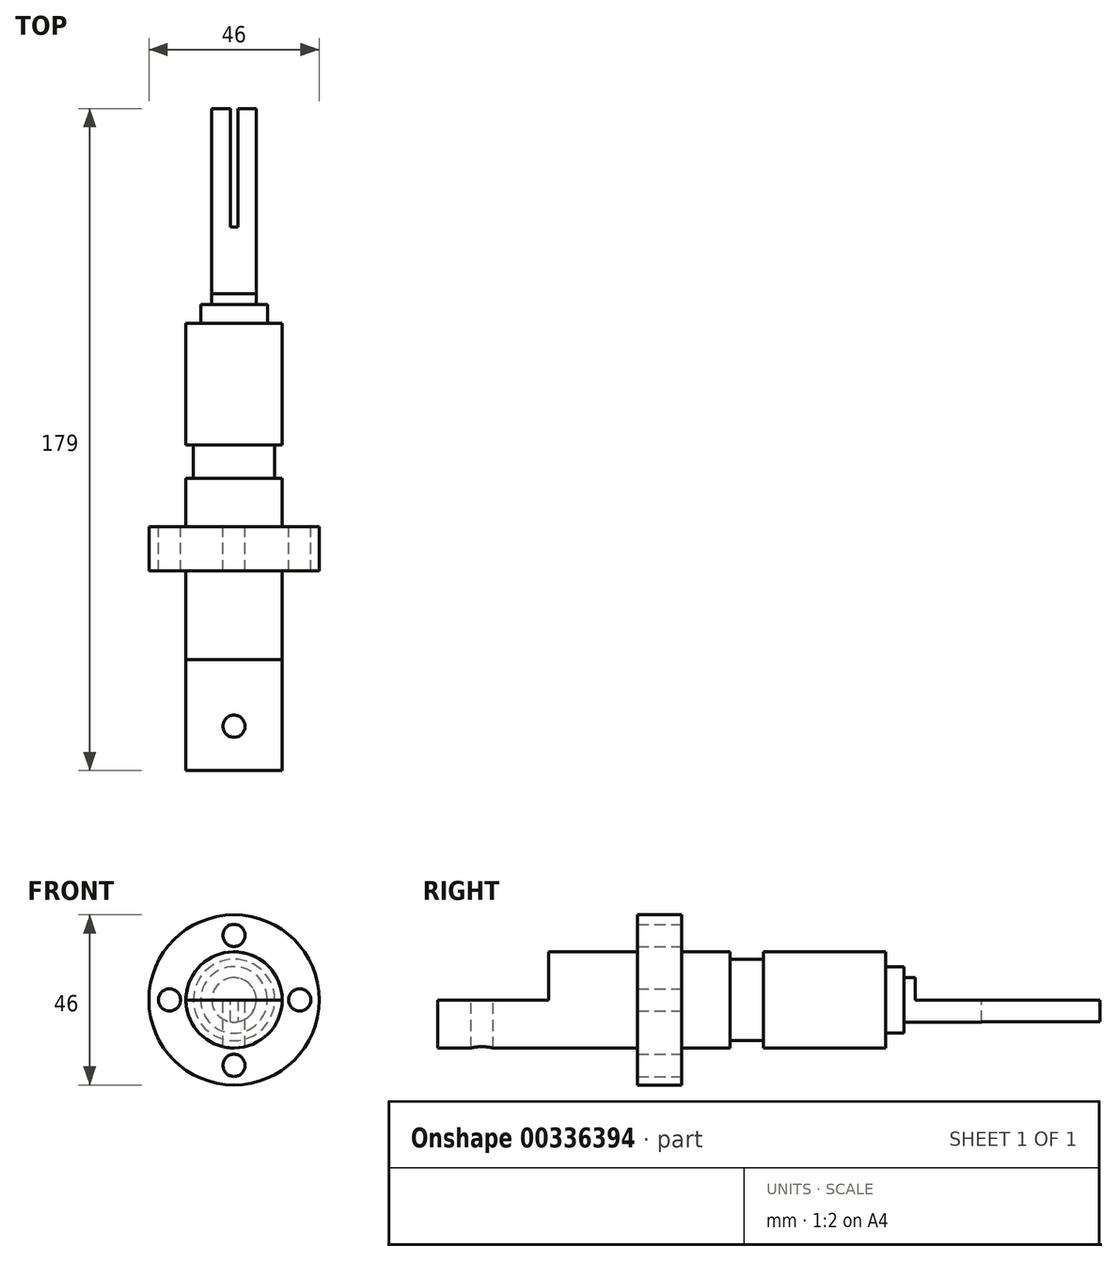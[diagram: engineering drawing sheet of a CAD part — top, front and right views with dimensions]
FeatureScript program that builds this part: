
annotation { "Feature Type Name" : "Feature", "Feature Type Description" : "" }
export const myFeature = defineFeature(function(context is Context, id is Id, definition is map)
    precondition{}
    {
        {
            var Q0;
            Q0=qCreatedBy(makeId("Front.planeOp"),FACE);
            var sketch = newSketch(context, id + "F0", { "sketchPlane" : qUnion([Q0])});
            skCircle(sketch, "E0", {"center": v(0, 0) * mm, "radius": 13 * mm});
            skSolve(sketch);
        }
        {
            var Q0;
            Q0 = qSketchRegion(id + "F0", true);
            extrude(context, id + "F1", {"entities" : qUnion([Q0]), "depth" : 54 * mm});
        }
        {
            var Q0;
            Q0=makeQuery(id+"F1.opExtrude","CAP_FACE",FACE,{"disambiguationData":[OSD([sQuery(id+"F0.wireOp",EDGE,"E0")])],"isStart":false});
            var sketch = newSketch(context, id + "F2", { "sketchPlane" : qUnion([Q0])});
            skLineSegment(sketch, "E1", {"start": v(0, 0) * mm, "end": v(13, 0) * mm});
            skLineSegment(sketch, "E2", {"start": v(13, 0) * mm, "end": v(-13, 0) * mm});
            skArc(sketch, "E3", {"start": v(13, 0) * mm, "mid": v(0, 13) * mm, "end": v(-13, 0) * mm});
            skSolve(sketch);
        }
        {
            var Q0;
            Q0 = qSketchRegion(id + "F2", true);
            extrude(context, id + "F3", {"entities" : qUnion([Q0]), "operationType" : NewBodyOperationType.REMOVE, "oppositeDirection" : true, "depth" : 30 * mm});
        }
        {
            var Q0;
            Q0=makeQuery(id+"F1.opExtrude","CAP_FACE",FACE,{"disambiguationData":[OSD([sQuery(id+"F0.wireOp",EDGE,"E0")])],"isStart":true});
            var sketch = newSketch(context, id + "F4", { "sketchPlane" : qUnion([Q0])});
            skCircle(sketch, "E4", {"center": v(0, 0) * mm, "radius": 23 * mm});
            skSolve(sketch);
        }
        {
            var Q0;
            Q0 = qSketchRegion(id + "F4", true);
            extrude(context, id + "F5", {"entities" : qUnion([Q0]), "operationType" : NewBodyOperationType.ADD, "depth" : 12 * mm});
        }
        {
            var Q0;
            Q0=makeQuery(id+"F5.opExtrude","CAP_FACE",FACE,{"disambiguationData":[OSD([sQuery(id+"F4.wireOp",EDGE,"E4")])],"isStart":false});
            var sketch = newSketch(context, id + "F6", { "sketchPlane" : qUnion([Q0])});
            skLineSegment(sketch, "E5", {"start": v(0, 0) * mm, "end": v(0, 23) * mm});
            skLineSegment(sketch, "E6", {"start": v(0, 23) * mm, "end": v(0, -23) * mm});
            skLineSegment(sketch, "E7", {"start": v(0, -23) * mm, "end": v(0, 0) * mm});
            skLineSegment(sketch, "E8", {"start": v(23, 0) * mm, "end": v(-23, 0) * mm});
            skCircle(sketch, "E9", {"center": v(0, 17.44) * mm, "radius": 3 * mm});
            skCircle(sketch, "E10", {"center": v(0, -17.71) * mm, "radius": 3 * mm});
            skCircle(sketch, "E11", {"center": v(-17.75, 0) * mm, "radius": 3 * mm});
            skCircle(sketch, "E12", {"center": v(17.45, 0) * mm, "radius": 3 * mm});
            skSolve(sketch);
        }
        {
            var Q0;
            Q0 = qSketchRegion(id + "F6", true);
            extrude(context, id + "F7", {"entities" : qUnion([Q0]), "operationType" : NewBodyOperationType.REMOVE, "oppositeDirection" : true, "depth" : 25 * mm});
        }
        {
            var Q0;
            Q0=makeQuery(id+"F5.opExtrude","CAP_FACE",FACE,{"disambiguationData":[OSD([sQuery(id+"F4.wireOp",EDGE,"E4")])],"isStart":false});
            var sketch = newSketch(context, id + "F8", { "sketchPlane" : qUnion([Q0])});
            skCircle(sketch, "E13", {"center": v(0, 0) * mm, "radius": 13 * mm});
            skSolve(sketch);
        }
        {
            var Q0;
            Q0 = qSketchRegion(id + "F8", true);
            extrude(context, id + "F9", {"entities" : qUnion([Q0]), "operationType" : NewBodyOperationType.ADD, "depth" : 13 * mm});
        }
        {
            var Q0;
            Q0=makeQuery(id+"F9.opExtrude","CAP_FACE",FACE,{"disambiguationData":[OSD([sQuery(id+"F8.wireOp",EDGE,"E13")])],"isStart":false});
            var sketch = newSketch(context, id + "F10", { "sketchPlane" : qUnion([Q0])});
            skCircle(sketch, "E14", {"center": v(0, 0) * mm, "radius": 11 * mm});
            skSolve(sketch);
        }
        {
            var Q0;
            Q0 = qSketchRegion(id + "F10", true);
            extrude(context, id + "F11", {"entities" : qUnion([Q0]), "operationType" : NewBodyOperationType.ADD, "depth" : 9 * mm});
        }
        {
            var Q0;
            Q0=makeQuery(id+"F11.opExtrude","CAP_FACE",FACE,{"disambiguationData":[OSD([sQuery(id+"F10.wireOp",EDGE,"E14")])],"isStart":false});
            var sketch = newSketch(context, id + "F12", { "sketchPlane" : qUnion([Q0])});
            skCircle(sketch, "E15", {"center": v(0, 0) * mm, "radius": 13 * mm});
            skSolve(sketch);
        }
        {
            var Q0;
            Q0 = qSketchRegion(id + "F12", true);
            extrude(context, id + "F13", {"entities" : qUnion([Q0]), "operationType" : NewBodyOperationType.ADD, "depth" : 8 * mm});
        }
        {
            var Q0;
            Q0=makeQuery(id+"F13.opExtrude","CAP_FACE",FACE,{"disambiguationData":[OSD([sQuery(id+"F12.wireOp",EDGE,"E15")])],"isStart":false});
            var sketch = newSketch(context, id + "F14", { "sketchPlane" : qUnion([Q0])});
            skCircle(sketch, "E16", {"center": v(0, 0) * mm, "radius": 13 * mm});
            skSolve(sketch);
        }
        {
            var Q0;
            Q0 = qSketchRegion(id + "F14", true);
            extrude(context, id + "F15", {"entities" : qUnion([Q0]), "operationType" : NewBodyOperationType.ADD, "depth" : 25 * mm});
        }
        {
            var Q0;
            Q0=makeQuery(id+"F3.boolean.opBoolean","COPY",FACE,{"derivedFrom":makeQuery(id+"F3.opExtrude","SWEPT_FACE",FACE,{"disambiguationData":[OSD([sQuery(id+"F2.wireOp",EDGE,"E2")])]})});
            var sketch = newSketch(context, id + "F16", { "sketchPlane" : qUnion([Q0])});
            skLineSegment(sketch, "E17.bottom", {"start": v(-13, -24) * mm, "end": v(13, -24) * mm, "construction": true});
            skLineSegment(sketch, "E17.top", {"start": v(-13, -54) * mm, "end": v(13, -54) * mm, "construction": true});
            skLineSegment(sketch, "E17.left", {"start": v(-13, -24) * mm, "end": v(-13, -54) * mm, "construction": true});
            skLineSegment(sketch, "E17.right", {"start": v(13, -24) * mm, "end": v(13, -54) * mm, "construction": true});
            skLineSegment(sketch, "E18", {"start": v(0, -24) * mm, "end": v(0, -54) * mm, "construction": true});
            skLineSegment(sketch, "E19", {"start": v(0, -54) * mm, "end": v(0, -42) * mm});
            skCircle(sketch, "E20", {"center": v(0, -42) * mm, "radius": 3 * mm});
            skSolve(sketch);
        }
        {
            var Q0;
            Q0 = qSketchRegion(id + "F16", true);
            extrude(context, id + "F17", {"entities" : qUnion([Q0]), "operationType" : NewBodyOperationType.REMOVE, "oppositeDirection" : true, "depth" : 14 * mm});
        }
        {
            var Q0;
            Q0=makeQuery(id+"F15.opExtrude","CAP_FACE",FACE,{"disambiguationData":[OSD([sQuery(id+"F14.wireOp",EDGE,"E16")])],"isStart":false});
            var sketch = newSketch(context, id + "F18", { "sketchPlane" : qUnion([Q0])});
            skCircle(sketch, "E21", {"center": v(0, 0) * mm, "radius": 9 * mm});
            skSolve(sketch);
        }
        {
            var Q0;
            Q0 = qSketchRegion(id + "F18", true);
            extrude(context, id + "F19", {"entities" : qUnion([Q0]), "operationType" : NewBodyOperationType.ADD, "depth" : 5 * mm});
        }
        {
            var Q0;
            Q0=makeQuery(id+"F19.opExtrude","CAP_FACE",FACE,{"disambiguationData":[OSD([sQuery(id+"F18.wireOp",EDGE,"E21")])],"isStart":false});
            var sketch = newSketch(context, id + "F20", { "sketchPlane" : qUnion([Q0])});
            skCircle(sketch, "E22", {"center": v(0, 0) * mm, "radius": 6 * mm});
            skSolve(sketch);
        }
        {
            var Q0;
            Q0 = qSketchRegion(id + "F20", true);
            extrude(context, id + "F21", {"entities" : qUnion([Q0]), "operationType" : NewBodyOperationType.ADD, "depth" : 53 * mm});
        }
        {
            var Q0;
            Q0=makeQuery(id+"F21.opExtrude","CAP_FACE",FACE,{"disambiguationData":[OSD([sQuery(id+"F20.wireOp",EDGE,"E22")])],"isStart":false});
            var sketch = newSketch(context, id + "F22", { "sketchPlane" : qUnion([Q0])});
            skArc(sketch, "E23", {"start": v(6, 0) * mm, "mid": v(0, 6) * mm, "end": v(-6, 0) * mm});
            skLineSegment(sketch, "E24", {"start": v(0, 0) * mm, "end": v(6, 0) * mm});
            skLineSegment(sketch, "E25", {"start": v(6, 0) * mm, "end": v(-6, 0) * mm});
            skSolve(sketch);
        }
        {
            var Q0;
            Q0 = qSketchRegion(id + "F22", true);
            extrude(context, id + "F23", {"entities" : qUnion([Q0]), "operationType" : NewBodyOperationType.REMOVE, "oppositeDirection" : true, "depth" : 50 * mm});
        }
        {
            var Q0;
            Q0=makeQuery(id+"F21.opExtrude","CAP_FACE",FACE,{"disambiguationData":[OSD([sQuery(id+"F20.wireOp",EDGE,"E22")])],"isStart":false});
            var sketch = newSketch(context, id + "F24", { "sketchPlane" : qUnion([Q0])});
            skLineSegment(sketch, "E26", {"start": v(0, 0) * mm, "end": v(1, 0) * mm});
            skLineSegment(sketch, "E27", {"start": v(0, 0) * mm, "end": v(-1, 0) * mm});
            skLineSegment(sketch, "E28", {"start": v(-1, 0) * mm, "end": v(-1, -7.18) * mm});
            skLineSegment(sketch, "E29", {"start": v(-1, -7.18) * mm, "end": v(1, -7.18) * mm});
            skLineSegment(sketch, "E30", {"start": v(1, -7.18) * mm, "end": v(1, 0) * mm});
            skSolve(sketch);
        }
        {
            var Q0;
            Q0 = qSketchRegion(id + "F24", true);
            extrude(context, id + "F25", {"entities" : qUnion([Q0]), "operationType" : NewBodyOperationType.REMOVE, "oppositeDirection" : true, "depth" : 32 * mm});
        }
    });
